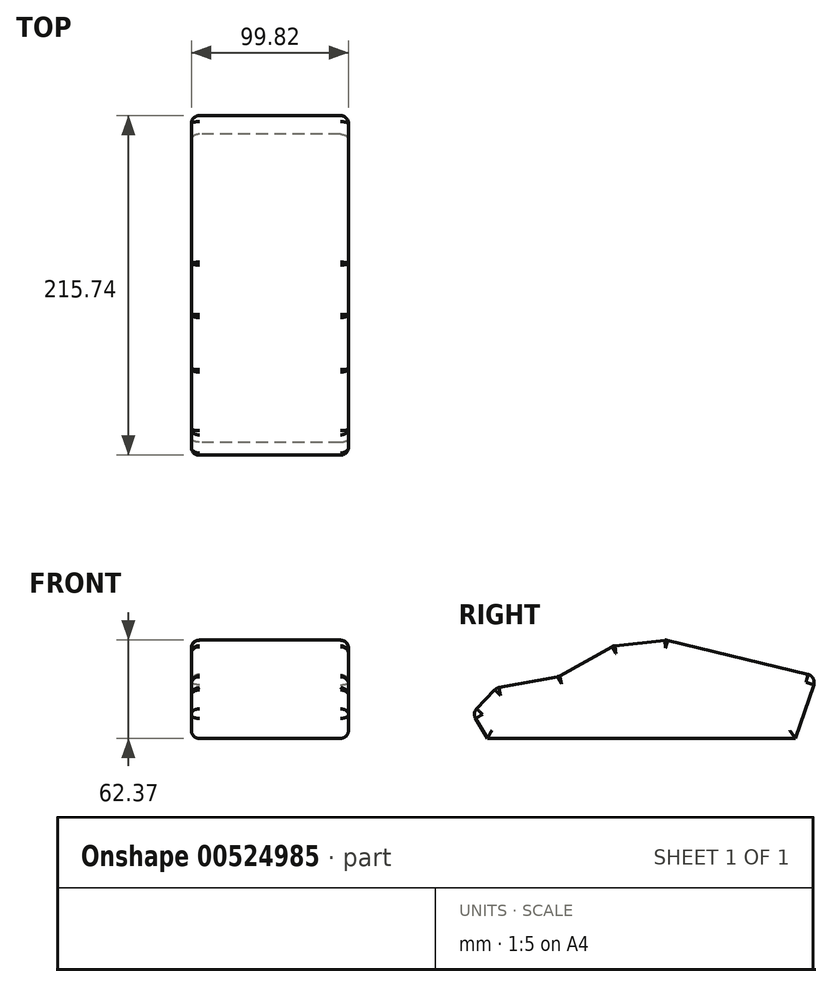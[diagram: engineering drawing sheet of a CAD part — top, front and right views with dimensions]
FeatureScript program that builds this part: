
annotation { "Feature Type Name" : "Feature", "Feature Type Description" : "" }
export const myFeature = defineFeature(function(context is Context, id is Id, definition is map)
    precondition{}
    {
        {
            var Q0;
            Q0=qCreatedBy(makeId("Right.planeOp"),FACE);
            var sketch = newSketch(context, id + "F0", { "sketchPlane" : qUnion([Q0])});
            skLineSegment(sketch, "E0", {"start": v(-72.84, 0) * mm, "end": v(-82.32, 15.96) * mm});
            skLineSegment(sketch, "E1", {"start": v(-82.32, 15.96) * mm, "end": v(-67.06, 31.91) * mm});
            skLineSegment(sketch, "E2", {"start": v(-67.06, 31.91) * mm, "end": v(-27.52, 39.31) * mm});
            skLineSegment(sketch, "E3", {"start": v(-27.52, 39.31) * mm, "end": v(7.17, 58.74) * mm});
            skLineSegment(sketch, "E4", {"start": v(7.17, 58.74) * mm, "end": v(40.7, 62.44) * mm});
            skLineSegment(sketch, "E5", {"start": v(40.7, 62.44) * mm, "end": v(136.2, 39.31) * mm});
            skLineSegment(sketch, "E6", {"start": v(136.2, 39.31) * mm, "end": v(122.79, 0) * mm});
            skLineSegment(sketch, "E7", {"start": v(122.79, 0) * mm, "end": v(-72.84, 0) * mm});
            skSolve(sketch);
        }
        {
            var Q0;
            Q0=makeQuery(id+"F0.imprint","IMPRINT",FACE,{"disambiguationData":[TD([[makeQuery(id+"F0.imprint","IMPRINT",EDGE,{"derivedFrom":sQuery(id+"F0.wireOp",EDGE,"E0")}),-1.0]])]});
            extrude(context, id + "F1", {"entities" : qUnion([Q0]), "depth" : 99.82 * mm, "offsetDistance" : 25.4 * mm});
        }
        {
            var Q0;
            Q0=makeQuery(id+"F1.opExtrude","CAP_FACE",FACE,{"disambiguationData":[OSD([sQuery(id+"F0.wireOp",EDGE,"E0"),sQuery(id+"F0.wireOp",EDGE,"E1"),sQuery(id+"F0.wireOp",EDGE,"E2"),sQuery(id+"F0.wireOp",EDGE,"E3"),sQuery(id+"F0.wireOp",EDGE,"E4"),sQuery(id+"F0.wireOp",EDGE,"E5"),sQuery(id+"F0.wireOp",EDGE,"E6"),sQuery(id+"F0.wireOp",EDGE,"E7")])],"isStart":false});
            fillet(context, id + "F2", {"entities" : qUnion([Q0]), "radius" : 5.08 * mm, "tangentPropagation" : true, "allowEdgeOverflow" : false});
        }
        {
            var Q0;
            Q0=makeQuery(id+"F1.opExtrude","CAP_FACE",FACE,{"disambiguationData":[OSD([sQuery(id+"F0.wireOp",EDGE,"E0"),sQuery(id+"F0.wireOp",EDGE,"E1"),sQuery(id+"F0.wireOp",EDGE,"E2"),sQuery(id+"F0.wireOp",EDGE,"E3"),sQuery(id+"F0.wireOp",EDGE,"E4"),sQuery(id+"F0.wireOp",EDGE,"E5"),sQuery(id+"F0.wireOp",EDGE,"E6"),sQuery(id+"F0.wireOp",EDGE,"E7")])],"isStart":true});
            fillet(context, id + "F3", {"entities" : qUnion([Q0]), "radius" : 5.08 * mm, "tangentPropagation" : true, "allowEdgeOverflow" : false});
        }
        {
            var Q0;
            Q0=makeQuery(id+"F1.opExtrude","SWEPT_EDGE",EDGE,{"disambiguationData":[OSD([sQuery(id+"F0.wireOp",EDGE,"E1"),sQuery(id+"F0.wireOp",EDGE,"E2")])]});
            var Q1;
            Q1=makeQuery(id+"F1.opExtrude","SWEPT_EDGE",EDGE,{"disambiguationData":[OSD([sQuery(id+"F0.wireOp",EDGE,"E0"),sQuery(id+"F0.wireOp",EDGE,"E1")])]});
            var Q2;
            Q2=makeQuery(id+"F1.opExtrude","SWEPT_EDGE",EDGE,{"disambiguationData":[OSD([sQuery(id+"F0.wireOp",EDGE,"E2"),sQuery(id+"F0.wireOp",EDGE,"E3")])]});
            var Q3;
            Q3=makeQuery(id+"F1.opExtrude","SWEPT_EDGE",EDGE,{"disambiguationData":[OSD([sQuery(id+"F0.wireOp",EDGE,"E3"),sQuery(id+"F0.wireOp",EDGE,"E4")])]});
            var Q4;
            Q4=makeQuery(id+"F1.opExtrude","SWEPT_EDGE",EDGE,{"disambiguationData":[OSD([sQuery(id+"F0.wireOp",EDGE,"E4"),sQuery(id+"F0.wireOp",EDGE,"E5")])]});
            var Q5;
            Q5=makeQuery(id+"F1.opExtrude","SWEPT_EDGE",EDGE,{"disambiguationData":[OSD([sQuery(id+"F0.wireOp",EDGE,"E5"),sQuery(id+"F0.wireOp",EDGE,"E6")])]});
            fillet(context, id + "F4", {"entities" : qUnion([Q0, Q1, Q2, Q3, Q4, Q5]), "radius" : 5.08 * mm, "tangentPropagation" : true, "allowEdgeOverflow" : false});
        }
    });
